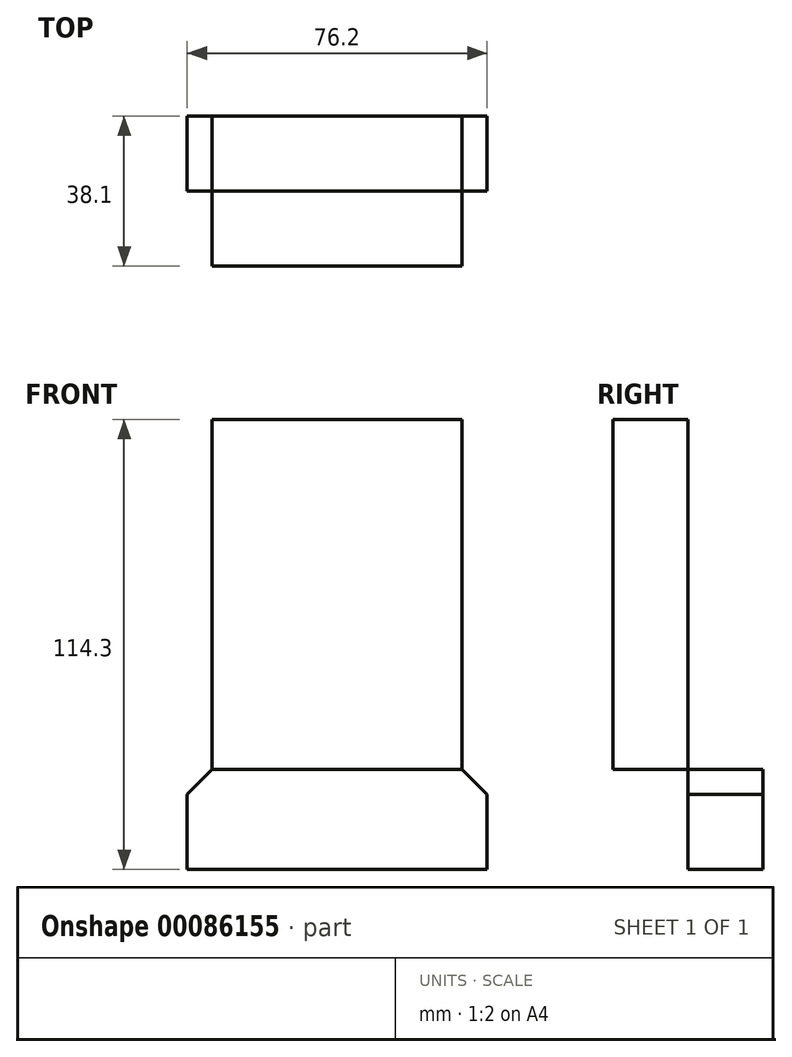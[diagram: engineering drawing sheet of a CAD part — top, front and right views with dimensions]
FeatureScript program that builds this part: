
annotation { "Feature Type Name" : "Feature", "Feature Type Description" : "" }
export const myFeature = defineFeature(function(context is Context, id is Id, definition is map)
    precondition{}
    {
        {
            var Q0;
            Q0=qCreatedBy(makeId("Top.planeOp"),FACE);
            var sketch = newSketch(context, id + "F0", { "sketchPlane" : qUnion([Q0])});
            skLineSegment(sketch, "E0.bottom", {"start": v(-30.23, 52.68) * mm, "end": v(45.97, 52.68) * mm});
            skLineSegment(sketch, "E0.top", {"start": v(-30.23, -48.92) * mm, "end": v(45.97, -48.92) * mm});
            skLineSegment(sketch, "E0.left", {"start": v(-30.23, 52.68) * mm, "end": v(-30.23, -48.92) * mm});
            skLineSegment(sketch, "E0.right", {"start": v(45.97, 52.68) * mm, "end": v(45.97, -48.92) * mm});
            skLineSegment(sketch, "E1.top", {"start": v(-30.23, 1.88) * mm, "end": v(45.97, 1.88) * mm});
            skLineSegment(sketch, "E1.left", {"start": v(-30.23, -48.92) * mm, "end": v(-30.23, 1.88) * mm});
            skLineSegment(sketch, "E1.right", {"start": v(45.97, -48.92) * mm, "end": v(45.97, 1.88) * mm});
            skLineSegment(sketch, "E2.top", {"start": v(-30.23, 20.93) * mm, "end": v(45.97, 20.93) * mm});
            skLineSegment(sketch, "E2.left", {"start": v(-30.23, 1.88) * mm, "end": v(-30.23, 20.93) * mm});
            skLineSegment(sketch, "E2.right", {"start": v(45.97, 1.88) * mm, "end": v(45.97, 20.93) * mm});
            skLineSegment(sketch, "E3", {"start": v(7.87, 52.68) * mm, "end": v(7.87, -48.92) * mm});
            skLineSegment(sketch, "E4.bottom", {"start": v(-30.23, -48.92) * mm, "end": v(-14.35, -48.92) * mm});
            skLineSegment(sketch, "E4.top", {"start": v(-30.23, -33.05) * mm, "end": v(-14.35, -33.05) * mm});
            skLineSegment(sketch, "E4.left", {"start": v(-30.23, -48.92) * mm, "end": v(-30.23, -33.05) * mm});
            skLineSegment(sketch, "E4.right", {"start": v(-14.35, -48.92) * mm, "end": v(-14.35, -33.05) * mm});
            skCircle(sketch, "E5", {"center": v(-14.35, -33.05) * mm, "radius": 6.35 * mm});
            skLineSegment(sketch, "E6.bottom", {"start": v(45.97, -48.92) * mm, "end": v(30.1, -48.92) * mm});
            skLineSegment(sketch, "E6.top", {"start": v(45.97, -33.05) * mm, "end": v(30.1, -33.05) * mm});
            skLineSegment(sketch, "E6.left", {"start": v(45.97, -48.92) * mm, "end": v(45.97, -33.05) * mm});
            skLineSegment(sketch, "E6.right", {"start": v(30.1, -48.92) * mm, "end": v(30.1, -33.05) * mm});
            skLineSegment(sketch, "E7.bottom", {"start": v(45.97, 52.68) * mm, "end": v(30.1, 52.68) * mm});
            skLineSegment(sketch, "E7.top", {"start": v(45.97, 36.8) * mm, "end": v(30.1, 36.8) * mm});
            skLineSegment(sketch, "E7.left", {"start": v(45.97, 52.68) * mm, "end": v(45.97, 36.8) * mm});
            skLineSegment(sketch, "E7.right", {"start": v(30.1, 52.68) * mm, "end": v(30.1, 36.8) * mm});
            skLineSegment(sketch, "E8.bottom", {"start": v(-30.23, 52.68) * mm, "end": v(-14.35, 52.68) * mm});
            skLineSegment(sketch, "E8.top", {"start": v(-30.23, 36.8) * mm, "end": v(-14.35, 36.8) * mm});
            skLineSegment(sketch, "E8.left", {"start": v(-30.23, 52.68) * mm, "end": v(-30.23, 36.8) * mm});
            skLineSegment(sketch, "E8.right", {"start": v(-14.35, 52.68) * mm, "end": v(-14.35, 36.8) * mm});
            skCircle(sketch, "E9", {"center": v(-14.35, 36.8) * mm, "radius": 6.35 * mm});
            skCircle(sketch, "E10", {"center": v(30.1, 36.8) * mm, "radius": 6.35 * mm});
            skCircle(sketch, "E11", {"center": v(30.1, -33.05) * mm, "radius": 6.35 * mm});
            skSolve(sketch);
        }
        {
            var Q0;
            {var subQ5=sQuery(id+"F0.wireOp",EDGE,"E0.right");Q0=makeQuery(id+"F0.imprint","IMPRINT",FACE,{"disambiguationData":[TD([[makeQuery(id+"F0.imprint","IMPRINT",EDGE,{"derivedFrom":subQ5}),-1.0]])]});}
            var Q1;
            {var subQ1=sQuery(id+"F0.wireOp",EDGE,"E7.bottom");Q1=makeQuery(id+"F0.imprint","IMPRINT",FACE,{"disambiguationData":[TD([[makeQuery(id+"F0.imprint","IMPRINT",EDGE,{"derivedFrom":subQ1}),1.0]])]});}
            var Q2;
            {var subQ5=sQuery(id+"F0.wireOp",EDGE,"E0.left");Q2=makeQuery(id+"F0.imprint","IMPRINT",FACE,{"disambiguationData":[TD([[makeQuery(id+"F0.imprint","IMPRINT",EDGE,{"derivedFrom":subQ5}),1.0]])]});}
            var Q3;
            {var subQ1=sQuery(id+"F0.wireOp",EDGE,"E8.bottom");Q3=makeQuery(id+"F0.imprint","IMPRINT",FACE,{"disambiguationData":[TD([[makeQuery(id+"F0.imprint","IMPRINT",EDGE,{"derivedFrom":subQ1}),-1.0]])]});}
            var Q4;
            {var subQ7=sQuery(id+"F0.wireOp",EDGE,"E1.right");Q4=makeQuery(id+"F0.imprint","IMPRINT",FACE,{"disambiguationData":[TD([[makeQuery(id+"F0.imprint","IMPRINT",EDGE,{"derivedFrom":subQ7}),1.0]])]});}
            var Q5;
            {var subQ5=sQuery(id+"F0.wireOp",EDGE,"E1.left");Q5=makeQuery(id+"F0.imprint","IMPRINT",FACE,{"disambiguationData":[TD([[makeQuery(id+"F0.imprint","IMPRINT",EDGE,{"derivedFrom":subQ5}),-1.0]])]});}
            var Q6;
            {var subQ1=sQuery(id+"F0.wireOp",EDGE,"E4.bottom");Q6=makeQuery(id+"F0.imprint","IMPRINT",FACE,{"disambiguationData":[TD([[makeQuery(id+"F0.imprint","IMPRINT",EDGE,{"derivedFrom":subQ1}),1.0]])]});}
            var Q7;
            {var subQ1=sQuery(id+"F0.wireOp",EDGE,"E6.bottom");Q7=makeQuery(id+"F0.imprint","IMPRINT",FACE,{"disambiguationData":[TD([[makeQuery(id+"F0.imprint","IMPRINT",EDGE,{"derivedFrom":subQ1}),-1.0]])]});}
            var Q8;
            {var subQ0=sQuery(id+"F0.wireOp",EDGE,"E2.left");Q8=makeQuery(id+"F0.imprint","IMPRINT",FACE,{"disambiguationData":[TD([[makeQuery(id+"F0.imprint","IMPRINT",EDGE,{"derivedFrom":subQ0}),-1.0]])]});}
            var Q9;
            {var subQ0=sQuery(id+"F0.wireOp",EDGE,"E2.right");Q9=makeQuery(id+"F0.imprint","IMPRINT",FACE,{"disambiguationData":[TD([[makeQuery(id+"F0.imprint","IMPRINT",EDGE,{"derivedFrom":subQ0}),1.0]])]});}
            extrude(context, id + "F1", {"entities" : qUnion([Q0, Q1, Q2, Q3, Q4, Q5, Q6, Q7, Q8, Q9]), "depth" : 25.4 * mm});
        }
        {
            var Q0;
            Q0=makeQuery(id+"F1.opExtrude","CAP_EDGE",EDGE,{"disambiguationData":[OSD([sQuery(id+"F0.wireOp",EDGE,"E0.bottom"),sQuery(id+"F0.wireOp",EDGE,"E7.bottom"),sQuery(id+"F0.wireOp",EDGE,"E8.bottom")])],"isStart":false});
            var Q1;
            Q1=makeQuery(id+"F1.opExtrude","CAP_EDGE",EDGE,{"disambiguationData":[OSD([sQuery(id+"F0.wireOp",EDGE,"E0.left"),sQuery(id+"F0.wireOp",EDGE,"E1.left"),sQuery(id+"F0.wireOp",EDGE,"E2.left"),sQuery(id+"F0.wireOp",EDGE,"E4.left"),sQuery(id+"F0.wireOp",EDGE,"E8.left")])],"isStart":false});
            var Q2;
            Q2=makeQuery(id+"F1.opExtrude","CAP_EDGE",EDGE,{"disambiguationData":[OSD([sQuery(id+"F0.wireOp",EDGE,"E0.top"),sQuery(id+"F0.wireOp",EDGE,"E4.bottom"),sQuery(id+"F0.wireOp",EDGE,"E6.bottom")])],"isStart":false});
            var Q3;
            Q3=makeQuery(id+"F1.opExtrude","CAP_EDGE",EDGE,{"disambiguationData":[OSD([sQuery(id+"F0.wireOp",EDGE,"E0.right"),sQuery(id+"F0.wireOp",EDGE,"E1.right"),sQuery(id+"F0.wireOp",EDGE,"E2.right"),sQuery(id+"F0.wireOp",EDGE,"E6.left"),sQuery(id+"F0.wireOp",EDGE,"E7.left")])],"isStart":false});
            chamfer(context, id + "F2", {"entities" : qUnion([Q0, Q1, Q2, Q3]), "width" : 6.35 * mm, "tangentPropagation" : true});
        }
        {
            var Q0;
            Q0=makeQuery(id+"F1.opExtrude","CAP_FACE",FACE,{"disambiguationData":[OSD([sQuery(id+"F0.wireOp",EDGE,"E0.bottom"),sQuery(id+"F0.wireOp",EDGE,"E0.left"),sQuery(id+"F0.wireOp",EDGE,"E0.right"),sQuery(id+"F0.wireOp",EDGE,"E0.top"),sQuery(id+"F0.wireOp",EDGE,"E1.left"),sQuery(id+"F0.wireOp",EDGE,"E1.right"),sQuery(id+"F0.wireOp",EDGE,"E2.left"),sQuery(id+"F0.wireOp",EDGE,"E2.right"),sQuery(id+"F0.wireOp",EDGE,"E4.bottom"),sQuery(id+"F0.wireOp",EDGE,"E4.left"),sQuery(id+"F0.wireOp",EDGE,"E5"),sQuery(id+"F0.wireOp",EDGE,"E6.bottom"),sQuery(id+"F0.wireOp",EDGE,"E6.left"),sQuery(id+"F0.wireOp",EDGE,"E7.bottom"),sQuery(id+"F0.wireOp",EDGE,"E7.left"),sQuery(id+"F0.wireOp",EDGE,"E8.bottom"),sQuery(id+"F0.wireOp",EDGE,"E8.left"),sQuery(id+"F0.wireOp",EDGE,"E9"),sQuery(id+"F0.wireOp",EDGE,"E10"),sQuery(id+"F0.wireOp",EDGE,"E11")])],"isStart":false});
            var sketch = newSketch(context, id + "F3", { "sketchPlane" : qUnion([Q0])});
            skLineSegment(sketch, "E12.bottom", {"start": v(-23.88, 1.88) * mm, "end": v(39.62, 1.88) * mm});
            skLineSegment(sketch, "E12.top", {"start": v(-23.88, -17.17) * mm, "end": v(39.62, -17.17) * mm});
            skLineSegment(sketch, "E12.left", {"start": v(-23.88, 1.88) * mm, "end": v(-23.88, -17.17) * mm});
            skLineSegment(sketch, "E12.right", {"start": v(39.62, 1.88) * mm, "end": v(39.62, -17.17) * mm});
            skSolve(sketch);
        }
        {
            var Q0;
            Q0 = qSketchRegion(id + "F3", true);
            extrude(context, id + "F4", {"entities" : qUnion([Q0]), "operationType" : NewBodyOperationType.ADD, "depth" : 88.9 * mm});
        }
    });
